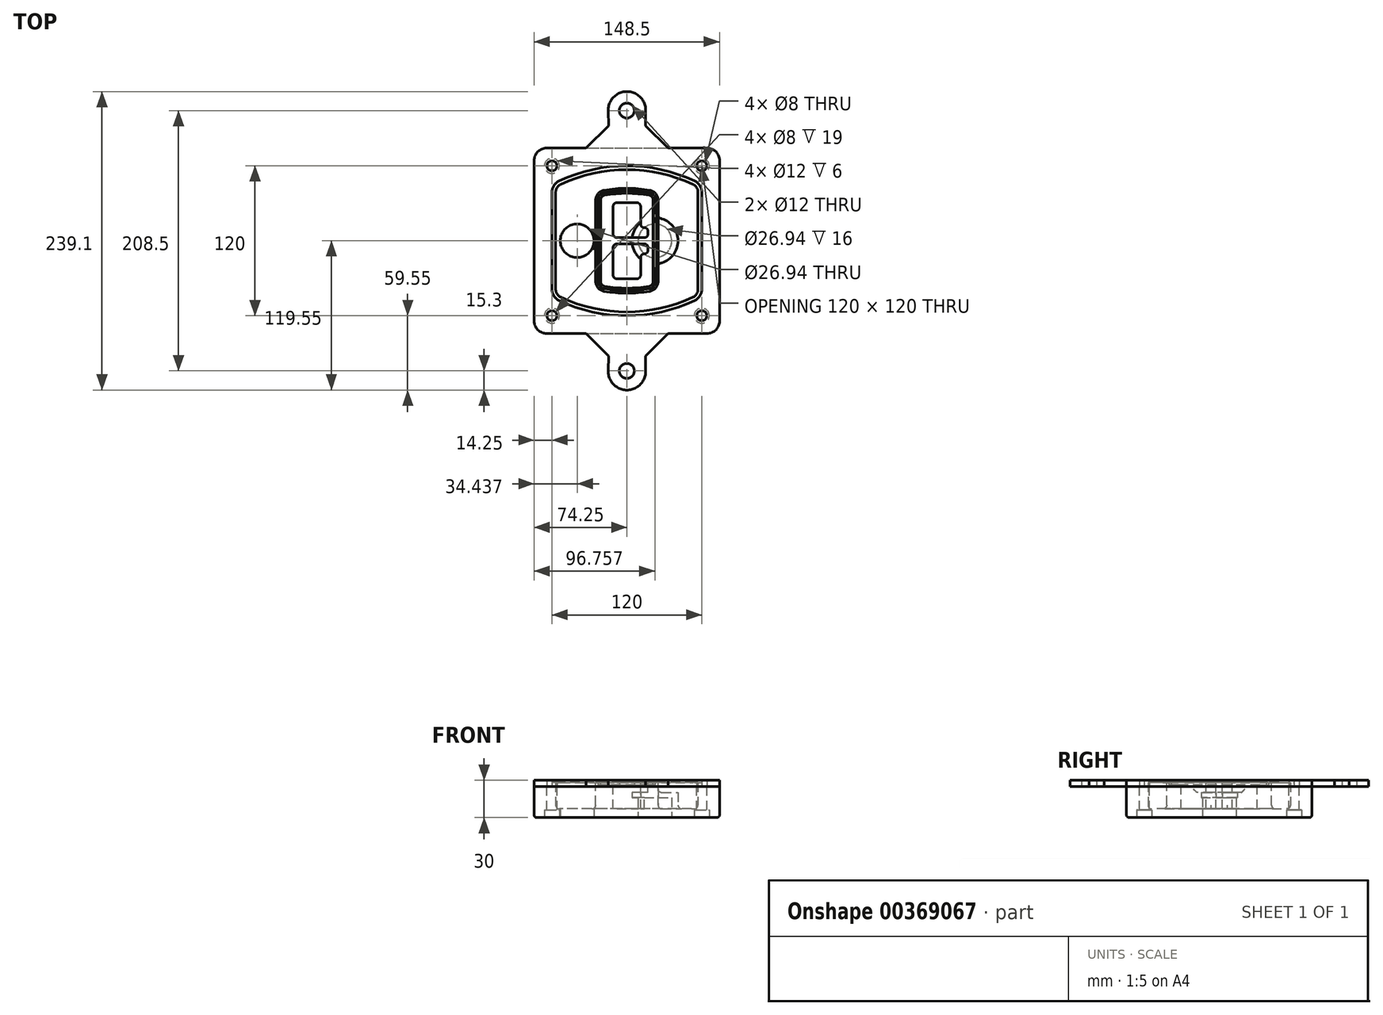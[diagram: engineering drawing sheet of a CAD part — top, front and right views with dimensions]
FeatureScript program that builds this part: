
annotation { "Feature Type Name" : "Feature", "Feature Type Description" : "" }
export const myFeature = defineFeature(function(context is Context, id is Id, definition is map)
    precondition{}
    {
        {
            var Q0;
            Q0=qCreatedBy(makeId("Top.planeOp"),FACE);
            var sketch = newSketch(context, id + "F0", { "sketchPlane" : qUnion([Q0])});
            skPoint(sketch, "E0.rect.middle", {"position": v(0, 0) * mm});
            skLineSegment(sketch, "E1.bottom", {"start": v(-64.25, -74.25) * mm, "end": v(64.25, -74.25) * mm});
            skLineSegment(sketch, "E1.top", {"start": v(-64.25, 74.25) * mm, "end": v(64.25, 74.25) * mm});
            skLineSegment(sketch, "E1.left", {"start": v(-74.25, -64.25) * mm, "end": v(-74.25, 64.25) * mm});
            skLineSegment(sketch, "E1.right", {"start": v(74.25, -64.25) * mm, "end": v(74.25, 64.25) * mm});
            skLineSegment(sketch, "E2", {"start": v(-74.25, 74.25) * mm, "end": v(74.25, -74.25) * mm, "construction": true});
            skLineSegment(sketch, "E3", {"start": v(74.25, 74.25) * mm, "end": v(-74.25, -74.25) * mm, "construction": true});
            skCircle(sketch, "E4", {"center": v(-60, 60) * mm, "radius": 4 * mm});
            skCircle(sketch, "E5", {"center": v(60, 60) * mm, "radius": 4 * mm});
            skCircle(sketch, "E6", {"center": v(60, -60) * mm, "radius": 4 * mm});
            skCircle(sketch, "E7", {"center": v(-60, -60) * mm, "radius": 4 * mm});
            skLineSegment(sketch, "E8", {"start": v(-60, 60) * mm, "end": v(60, 60) * mm, "construction": true});
            skLineSegment(sketch, "E9", {"start": v(60, 60) * mm, "end": v(60, -60) * mm, "construction": true});
            skLineSegment(sketch, "E10", {"start": v(60, -60) * mm, "end": v(-60, -60) * mm, "construction": true});
            skLineSegment(sketch, "E11", {"start": v(-60, -60) * mm, "end": v(-60, 60) * mm, "construction": true});
            skLineSegment(sketch, "E12", {"start": v(-60, 38.83) * mm, "end": v(-60, -38.83) * mm});
            skLineSegment(sketch, "E13", {"start": v(60, 38.83) * mm, "end": v(60, -38.83) * mm});
            skArc(sketch, "E14", {"start": v(54.26, 47.88) * mm, "mid": v(0, 60) * mm, "end": v(-54.26, 47.88) * mm});
            skArc(sketch, "E15", {"start": v(-54.26, -47.88) * mm, "mid": v(0, -60) * mm, "end": v(54.26, -47.88) * mm});
            skLineSegment(sketch, "E16", {"start": v(-60, 0) * mm, "end": v(60, 0) * mm, "construction": true});
            skPoint(sketch, "E17.visualSharp", {"position": v(-60, -45) * mm});
            skArc(sketch, "E17.filletArc", {"start": v(-60, -38.83) * mm, "mid": v(-58.44, -44.2) * mm, "end": v(-54.26, -47.88) * mm});
            skPoint(sketch, "E18.visualSharp", {"position": v(-60, 45) * mm});
            skArc(sketch, "E18.filletArc", {"start": v(-54.26, 47.88) * mm, "mid": v(-58.44, 44.2) * mm, "end": v(-60, 38.83) * mm});
            skPoint(sketch, "E19.visualSharp", {"position": v(60, 45) * mm});
            skArc(sketch, "E19.filletArc", {"start": v(60, 38.83) * mm, "mid": v(58.44, 44.2) * mm, "end": v(54.26, 47.88) * mm});
            skPoint(sketch, "E20.visualSharp", {"position": v(60, -45) * mm});
            skArc(sketch, "E20.filletArc", {"start": v(54.26, -47.88) * mm, "mid": v(58.44, -44.2) * mm, "end": v(60, -38.83) * mm});
            skPoint(sketch, "E21.visualSharp", {"position": v(-74.25, 74.25) * mm});
            skArc(sketch, "E21.filletArc", {"start": v(-64.25, 74.25) * mm, "mid": v(-71.32, 71.32) * mm, "end": v(-74.25, 64.25) * mm});
            skPoint(sketch, "E22.visualSharp", {"position": v(74.25, 74.25) * mm});
            skArc(sketch, "E22.filletArc", {"start": v(74.25, 64.25) * mm, "mid": v(71.32, 71.32) * mm, "end": v(64.25, 74.25) * mm});
            skPoint(sketch, "E23.visualSharp", {"position": v(74.25, -74.25) * mm});
            skArc(sketch, "E23.filletArc", {"start": v(64.25, -74.25) * mm, "mid": v(71.32, -71.32) * mm, "end": v(74.25, -64.25) * mm});
            skPoint(sketch, "E24.visualSharp", {"position": v(-74.25, -74.25) * mm});
            skArc(sketch, "E24.filletArc", {"start": v(-74.25, -64.25) * mm, "mid": v(-71.32, -71.32) * mm, "end": v(-64.25, -74.25) * mm});
            skArc(sketch, "E25.0", {"start": v(57, 38.83) * mm, "mid": v(55.9, 42.58) * mm, "end": v(52.98, 45.17) * mm});
            skLineSegment(sketch, "E25.1", {"start": v(57, 38.83) * mm, "end": v(57, -38.83) * mm});
            skArc(sketch, "E25.2", {"start": v(52.98, -45.17) * mm, "mid": v(55.9, -42.58) * mm, "end": v(57, -38.83) * mm});
            skArc(sketch, "E25.3", {"start": v(-52.98, -45.17) * mm, "mid": v(0, -57) * mm, "end": v(52.98, -45.17) * mm});
            skArc(sketch, "E25.4", {"start": v(-57, -38.83) * mm, "mid": v(-55.9, -42.58) * mm, "end": v(-52.98, -45.17) * mm});
            skArc(sketch, "E25.5", {"start": v(52.98, 45.17) * mm, "mid": v(0, 57) * mm, "end": v(-52.98, 45.17) * mm});
            skLineSegment(sketch, "E25.6", {"start": v(-57, 38.83) * mm, "end": v(-57, -38.83) * mm});
            skArc(sketch, "E25.7", {"start": v(-52.98, 45.17) * mm, "mid": v(-55.9, 42.58) * mm, "end": v(-57, 38.83) * mm});
            skArc(sketch, "E26.0", {"start": v(-55.96, 51.5) * mm, "mid": v(-61.82, 46.33) * mm, "end": v(-64, 38.83) * mm});
            skArc(sketch, "E26.1", {"start": v(55.96, 51.5) * mm, "mid": v(0, 64) * mm, "end": v(-55.96, 51.5) * mm});
            skArc(sketch, "E26.2", {"start": v(64, 38.83) * mm, "mid": v(61.82, 46.33) * mm, "end": v(55.96, 51.5) * mm});
            skLineSegment(sketch, "E26.3", {"start": v(64, 38.83) * mm, "end": v(64, -38.83) * mm});
            skArc(sketch, "E26.4", {"start": v(55.96, -51.5) * mm, "mid": v(61.82, -46.33) * mm, "end": v(64, -38.83) * mm});
            skLineSegment(sketch, "E26.5", {"start": v(-64, 38.83) * mm, "end": v(-64, -38.83) * mm});
            skArc(sketch, "E26.6", {"start": v(-55.96, -51.5) * mm, "mid": v(0, -64) * mm, "end": v(55.96, -51.5) * mm});
            skArc(sketch, "E26.7", {"start": v(-64, -38.83) * mm, "mid": v(-61.82, -46.33) * mm, "end": v(-55.96, -51.5) * mm});
            skSolve(sketch);
        }
        {
            var Q0;
            Q0=makeQuery(id+"F0.imprint","IMPRINT",FACE,{"disambiguationData":[TD([[makeQuery(id+"F0.imprint","IMPRINT",EDGE,{"derivedFrom":sQuery(id+"F0.wireOp",EDGE,"E1.bottom")}),1.0]])]});
            var Q1;
            Q1=makeQuery(id+"F0.imprint","IMPRINT",FACE,{"disambiguationData":[TD([[makeQuery(id+"F0.imprint","IMPRINT",EDGE,{"derivedFrom":sQuery(id+"F0.wireOp",EDGE,"E12")}),1.0]])]});
            var Q2;
            Q2=makeQuery(id+"F0.imprint","IMPRINT",FACE,{"disambiguationData":[TD([[makeQuery(id+"F0.imprint","IMPRINT",EDGE,{"derivedFrom":sQuery(id+"F0.wireOp",EDGE,"E25.0")}),1.0]])]});
            var Q3;
            Q3=makeQuery(id+"F0.imprint","IMPRINT",FACE,{"disambiguationData":[TD([[makeQuery(id+"F0.imprint","IMPRINT",EDGE,{"derivedFrom":sQuery(id+"F0.wireOp",EDGE,"E12")}),-1.0]])]});
            extrude(context, id + "F1", {"entities" : qUnion([Q0, Q1, Q2, Q3]), "oppositeDirection" : true, "depth" : 25 * mm});
        }
        {
            var Q0;
            Q0=makeQuery(id+"F0.imprint","IMPRINT",FACE,{"disambiguationData":[TD([[makeQuery(id+"F0.imprint","IMPRINT",EDGE,{"derivedFrom":sQuery(id+"F0.wireOp",EDGE,"E12")}),1.0]])]});
            extrude(context, id + "F2", {"entities" : qUnion([Q0]), "operationType" : NewBodyOperationType.ADD, "depth" : 3 * mm});
        }
        {
            var Q0;
            Q0=makeQuery(id+"F0.imprint","IMPRINT",FACE,{"disambiguationData":[TD([[makeQuery(id+"F0.imprint","IMPRINT",EDGE,{"derivedFrom":sQuery(id+"F0.wireOp",EDGE,"E25.0")}),1.0]])]});
            extrude(context, id + "F3", {"entities" : qUnion([Q0]), "operationType" : NewBodyOperationType.REMOVE, "oppositeDirection" : true, "depth" : 18 * mm});
        }
        {
            var Q0;
            Q0=makeQuery(id+"F2.opExtrude","CAP_FACE",FACE,{"disambiguationData":[OSD([sQuery(id+"F0.wireOp",EDGE,"E12"),sQuery(id+"F0.wireOp",EDGE,"E13"),sQuery(id+"F0.wireOp",EDGE,"E14"),sQuery(id+"F0.wireOp",EDGE,"E15"),sQuery(id+"F0.wireOp",EDGE,"E17.filletArc"),sQuery(id+"F0.wireOp",EDGE,"E18.filletArc"),sQuery(id+"F0.wireOp",EDGE,"E19.filletArc"),sQuery(id+"F0.wireOp",EDGE,"E20.filletArc"),sQuery(id+"F0.wireOp",EDGE,"E25.0"),sQuery(id+"F0.wireOp",EDGE,"E25.1"),sQuery(id+"F0.wireOp",EDGE,"E25.2"),sQuery(id+"F0.wireOp",EDGE,"E25.3"),sQuery(id+"F0.wireOp",EDGE,"E25.4"),sQuery(id+"F0.wireOp",EDGE,"E25.5"),sQuery(id+"F0.wireOp",EDGE,"E25.6"),sQuery(id+"F0.wireOp",EDGE,"E25.7")])],"isStart":false});
            var sketch = newSketch(context, id + "F4", { "sketchPlane" : qUnion([Q0])});
            skArc(sketch, "E27.0", {"start": v(-18.34, -40.45) * mm, "mid": v(0, -42) * mm, "end": v(18.34, -40.45) * mm});
            skArc(sketch, "E28.0", {"start": v(18.34, 40.45) * mm, "mid": v(0, 42) * mm, "end": v(-18.34, 40.45) * mm});
            skLineSegment(sketch, "E29", {"start": v(-25, 32.57) * mm, "end": v(-25, -32.57) * mm});
            skLineSegment(sketch, "E30", {"start": v(25, 32.57) * mm, "end": v(25, -32.57) * mm});
            skLineSegment(sketch, "E31", {"start": v(-25, 39.1) * mm, "end": v(25, 39.1) * mm, "construction": true});
            skLineSegment(sketch, "E32", {"start": v(-25, -39.1) * mm, "end": v(25, -39.1) * mm, "construction": true});
            skPoint(sketch, "E33.visualSharp", {"position": v(-25, 39.1) * mm});
            skArc(sketch, "E33.filletArc", {"start": v(-18.34, 40.45) * mm, "mid": v(-23.11, 37.73) * mm, "end": v(-25, 32.57) * mm});
            skPoint(sketch, "E34.visualSharp", {"position": v(25, 39.1) * mm});
            skArc(sketch, "E34.filletArc", {"start": v(25, 32.57) * mm, "mid": v(23.11, 37.73) * mm, "end": v(18.34, 40.45) * mm});
            skPoint(sketch, "E35.visualSharp", {"position": v(25, -39.1) * mm});
            skArc(sketch, "E35.filletArc", {"start": v(18.34, -40.45) * mm, "mid": v(23.11, -37.73) * mm, "end": v(25, -32.57) * mm});
            skPoint(sketch, "E36.visualSharp", {"position": v(-25, -39.1) * mm});
            skArc(sketch, "E36.filletArc", {"start": v(-25, -32.57) * mm, "mid": v(-23.11, -37.73) * mm, "end": v(-18.34, -40.45) * mm});
            skArc(sketch, "E37.0", {"start": v(52.98, 45.17) * mm, "mid": v(0, 57) * mm, "end": v(-52.98, 45.17) * mm});
            skArc(sketch, "E37.1", {"start": v(-52.98, 45.17) * mm, "mid": v(-55.9, 42.58) * mm, "end": v(-57, 38.83) * mm});
            skLineSegment(sketch, "E37.2", {"start": v(-57, 38.83) * mm, "end": v(-57, -38.83) * mm});
            skArc(sketch, "E37.3", {"start": v(-57, -38.83) * mm, "mid": v(-55.9, -42.58) * mm, "end": v(-52.98, -45.17) * mm});
            skArc(sketch, "E37.4", {"start": v(-52.98, -45.17) * mm, "mid": v(0, -57) * mm, "end": v(52.98, -45.17) * mm});
            skArc(sketch, "E37.5", {"start": v(52.98, -45.17) * mm, "mid": v(55.9, -42.58) * mm, "end": v(57, -38.83) * mm});
            skLineSegment(sketch, "E37.6", {"start": v(57, 38.83) * mm, "end": v(57, -38.83) * mm});
            skArc(sketch, "E37.7", {"start": v(57, 38.83) * mm, "mid": v(55.9, 42.58) * mm, "end": v(52.98, 45.17) * mm});
            skLineSegment(sketch, "E38.0", {"start": v(23, 32.57) * mm, "end": v(23, -32.57) * mm});
            skArc(sketch, "E38.1", {"start": v(18, -38.48) * mm, "mid": v(21.58, -36.44) * mm, "end": v(23, -32.57) * mm});
            skArc(sketch, "E38.2", {"start": v(-18, -38.48) * mm, "mid": v(0, -40) * mm, "end": v(18, -38.48) * mm});
            skArc(sketch, "E38.3", {"start": v(-23, -32.57) * mm, "mid": v(-21.58, -36.44) * mm, "end": v(-18, -38.48) * mm});
            skLineSegment(sketch, "E38.4", {"start": v(-23, 32.57) * mm, "end": v(-23, -32.57) * mm});
            skArc(sketch, "E38.5", {"start": v(23, 32.57) * mm, "mid": v(21.58, 36.44) * mm, "end": v(18, 38.48) * mm});
            skArc(sketch, "E38.6", {"start": v(-18, 38.48) * mm, "mid": v(-21.58, 36.44) * mm, "end": v(-23, 32.57) * mm});
            skArc(sketch, "E38.7", {"start": v(18, 38.48) * mm, "mid": v(0, 40) * mm, "end": v(-18, 38.48) * mm});
            skArc(sketch, "E39.0", {"start": v(21, 32.57) * mm, "mid": v(20.06, 35.15) * mm, "end": v(17.67, 36.5) * mm});
            skLineSegment(sketch, "E39.1", {"start": v(21, 32.57) * mm, "end": v(21, -32.57) * mm});
            skArc(sketch, "E39.2", {"start": v(17.67, -36.5) * mm, "mid": v(20.06, -35.15) * mm, "end": v(21, -32.57) * mm});
            skArc(sketch, "E39.3", {"start": v(-17.67, -36.5) * mm, "mid": v(0, -38) * mm, "end": v(17.67, -36.5) * mm});
            skArc(sketch, "E39.4", {"start": v(-21, -32.57) * mm, "mid": v(-20.06, -35.15) * mm, "end": v(-17.67, -36.5) * mm});
            skArc(sketch, "E39.5", {"start": v(17.67, 36.5) * mm, "mid": v(0, 38) * mm, "end": v(-17.67, 36.5) * mm});
            skLineSegment(sketch, "E39.6", {"start": v(-21, 32.57) * mm, "end": v(-21, -32.57) * mm});
            skArc(sketch, "E39.7", {"start": v(-17.67, 36.5) * mm, "mid": v(-20.06, 35.15) * mm, "end": v(-21, 32.57) * mm});
            skLineSegment(sketch, "E40", {"start": v(-25, 0) * mm, "end": v(25, 0) * mm, "construction": true});
            skLineSegment(sketch, "E41", {"start": v(-11, 5.5) * mm, "end": v(-11, 27.5) * mm});
            skLineSegment(sketch, "E42", {"start": v(-8, 30.5) * mm, "end": v(8, 30.5) * mm});
            skLineSegment(sketch, "E43", {"start": v(11, 27.5) * mm, "end": v(11, 13.5) * mm});
            skLineSegment(sketch, "E44", {"start": v(14, 10.5) * mm, "end": v(14, 10.5) * mm});
            skLineSegment(sketch, "E45", {"start": v(17, 7.5) * mm, "end": v(17, 5.5) * mm});
            skLineSegment(sketch, "E46", {"start": v(14, 2.5) * mm, "end": v(-8, 2.5) * mm});
            skPoint(sketch, "E47.visualSharp", {"position": v(-11, 30.5) * mm});
            skArc(sketch, "E47.filletArc", {"start": v(-8, 30.5) * mm, "mid": v(-10.12, 29.62) * mm, "end": v(-11, 27.5) * mm});
            skPoint(sketch, "E48.visualSharp", {"position": v(11, 30.5) * mm});
            skArc(sketch, "E48.filletArc", {"start": v(11, 27.5) * mm, "mid": v(10.12, 29.62) * mm, "end": v(8, 30.5) * mm});
            skPoint(sketch, "E49.visualSharp", {"position": v(11, 10.5) * mm});
            skArc(sketch, "E49.filletArc", {"start": v(11, 13.5) * mm, "mid": v(11.88, 11.38) * mm, "end": v(14, 10.5) * mm});
            skPoint(sketch, "E50.visualSharp", {"position": v(17, 10.5) * mm});
            skArc(sketch, "E50.filletArc", {"start": v(17, 7.5) * mm, "mid": v(16.12, 9.62) * mm, "end": v(14, 10.5) * mm});
            skPoint(sketch, "E51.visualSharp", {"position": v(17, 2.5) * mm});
            skArc(sketch, "E51.filletArc", {"start": v(14, 2.5) * mm, "mid": v(16.12, 3.38) * mm, "end": v(17, 5.5) * mm});
            skPoint(sketch, "E52.visualSharp", {"position": v(-11, 2.5) * mm});
            skArc(sketch, "E52.filletArc", {"start": v(-11, 5.5) * mm, "mid": v(-10.12, 3.38) * mm, "end": v(-8, 2.5) * mm});
            skLineSegment(sketch, "E53.0.MirrorCS", {"start": v(14, -2.5) * mm, "end": v(-8, -2.5) * mm});
            skArc(sketch, "E54.0.MirrorCS", {"start": v(-11, -5.5) * mm, "mid": v(-10.12, -3.38) * mm, "end": v(-8, -2.5) * mm});
            skLineSegment(sketch, "E55.0.MirrorCS", {"start": v(-11, -5.5) * mm, "end": v(-11, -27.5) * mm});
            skArc(sketch, "E56.0.MirrorCS", {"start": v(-8, -30.5) * mm, "mid": v(-10.12, -29.62) * mm, "end": v(-11, -27.5) * mm});
            skLineSegment(sketch, "E57.0.MirrorCS", {"start": v(-8, -30.5) * mm, "end": v(8, -30.5) * mm});
            skArc(sketch, "E58.0.MirrorCS", {"start": v(11, -27.5) * mm, "mid": v(10.12, -29.62) * mm, "end": v(8, -30.5) * mm});
            skLineSegment(sketch, "E59.0.MirrorCS", {"start": v(11, -27.5) * mm, "end": v(11, -13.5) * mm});
            skArc(sketch, "E60.0.MirrorCS", {"start": v(11, -13.5) * mm, "mid": v(11.88, -11.38) * mm, "end": v(14, -10.5) * mm});
            skArc(sketch, "E61.0.MirrorCS", {"start": v(17, -7.5) * mm, "mid": v(16.12, -9.62) * mm, "end": v(14, -10.5) * mm});
            skLineSegment(sketch, "E62.0.MirrorCS", {"start": v(17, -7.5) * mm, "end": v(17, -5.5) * mm});
            skArc(sketch, "E63.0.MirrorCS", {"start": v(14, -2.5) * mm, "mid": v(16.12, -3.38) * mm, "end": v(17, -5.5) * mm});
            skSolve(sketch);
        }
        {
            var Q0;
            Q0=makeQuery(id+"F4.imprint","IMPRINT",FACE,{"disambiguationData":[TD([[makeQuery(id+"F4.imprint","IMPRINT",EDGE,{"derivedFrom":sQuery(id+"F4.wireOp",EDGE,"E27.0")}),1.0]])]});
            var Q1;
            Q1=makeQuery(id+"F4.imprint","IMPRINT",FACE,{"disambiguationData":[TD([[makeQuery(id+"F4.imprint","IMPRINT",EDGE,{"derivedFrom":sQuery(id+"F4.wireOp",EDGE,"E38.0")}),-1.0]])]});
            var Q2;
            Q2=makeQuery(id+"F4.imprint","IMPRINT",FACE,{"disambiguationData":[TD([[makeQuery(id+"F4.imprint","IMPRINT",EDGE,{"derivedFrom":sQuery(id+"F4.wireOp",EDGE,"E39.0")}),1.0]])]});
            extrude(context, id + "F5", {"entities" : qUnion([Q0, Q1, Q2]), "operationType" : NewBodyOperationType.ADD, "endBound" : BoundingType.UP_TO_NEXT, "oppositeDirection" : true, "depth" : 25 * mm});
        }
        {
            var Q0;
            Q0=makeQuery(id+"F4.imprint","IMPRINT",FACE,{"disambiguationData":[TD([[makeQuery(id+"F4.imprint","IMPRINT",EDGE,{"derivedFrom":sQuery(id+"F4.wireOp",EDGE,"E38.0")}),-1.0]])]});
            extrude(context, id + "F6", {"entities" : qUnion([Q0]), "operationType" : NewBodyOperationType.REMOVE, "oppositeDirection" : true, "depth" : 2 * mm});
        }
        {
            var Q0;
            Q0=makeQuery(id+"F1.opExtrude","CAP_FACE",FACE,{"disambiguationData":[OSD([sQuery(id+"F0.wireOp",EDGE,"E1.bottom"),sQuery(id+"F0.wireOp",EDGE,"E1.top"),sQuery(id+"F0.wireOp",EDGE,"E1.left"),sQuery(id+"F0.wireOp",EDGE,"E1.right"),sQuery(id+"F0.wireOp",EDGE,"E4"),sQuery(id+"F0.wireOp",EDGE,"E5"),sQuery(id+"F0.wireOp",EDGE,"E6"),sQuery(id+"F0.wireOp",EDGE,"E7"),sQuery(id+"F0.wireOp",EDGE,"E21.filletArc"),sQuery(id+"F0.wireOp",EDGE,"E22.filletArc"),sQuery(id+"F0.wireOp",EDGE,"E23.filletArc"),sQuery(id+"F0.wireOp",EDGE,"E24.filletArc")])],"isStart":false});
            var sketch = newSketch(context, id + "F7", { "sketchPlane" : qUnion([Q0])});
            skCircle(sketch, "E64", {"center": v(22.5, 0) * mm, "radius": 13.47 * mm});
            skCircle(sketch, "E65", {"center": v(-39.81, 0) * mm, "radius": 13.47 * mm});
            skLineSegment(sketch, "E66", {"start": v(74.25, 0) * mm, "end": v(-74.25, 0) * mm});
            skCircle(sketch, "E67", {"center": v(22.5, 0) * mm, "radius": 18.47 * mm});
            skCircle(sketch, "E68", {"center": v(60, -60) * mm, "radius": 6 * mm});
            skCircle(sketch, "E69", {"center": v(-60, -60) * mm, "radius": 6 * mm});
            skCircle(sketch, "E70", {"center": v(-60, 60) * mm, "radius": 6 * mm});
            skCircle(sketch, "E71", {"center": v(60, 60) * mm, "radius": 6 * mm});
            skSolve(sketch);
        }
        {
            var Q0;
            {var subQ1=sQuery(id+"F7.wireOp",EDGE,"E66");var subQ4=sQuery(id+"F7.wireOp",EDGE,"E64");var subQ6=makeQuery(id+"F7.imprint","INTERSECT",VERTEX,{"disambiguationData":[OD(0.0)],"derivedFrom":[subQ4,subQ1]});Q0=makeQuery(id+"F7.imprint","IMPRINT",FACE,{"disambiguationData":[TD([[makeQuery(id+"F7.imprint","IMPRINT",EDGE,{"disambiguationData":[TD([[subQ6,-1.0]])],"derivedFrom":subQ4}),-1.0]])]});}
            var Q1;
            {var subQ0=sQuery(id+"F7.wireOp",EDGE,"E66");var subQ1=sQuery(id+"F7.wireOp",EDGE,"E64");var subQ3=makeQuery(id+"F7.imprint","INTERSECT",VERTEX,{"disambiguationData":[OD(0.0)],"derivedFrom":[subQ1,subQ0]});Q1=makeQuery(id+"F7.imprint","IMPRINT",FACE,{"disambiguationData":[TD([[makeQuery(id+"F7.imprint","IMPRINT",EDGE,{"disambiguationData":[TD([[subQ3,-1.0]])],"derivedFrom":subQ1}),1.0]])]});}
            var Q2;
            {var subQ0=sQuery(id+"F7.wireOp",EDGE,"E66");var subQ1=sQuery(id+"F7.wireOp",EDGE,"E64");var subQ3=makeQuery(id+"F7.imprint","INTERSECT",VERTEX,{"disambiguationData":[OD(0.0)],"derivedFrom":[subQ1,subQ0]});Q2=makeQuery(id+"F7.imprint","IMPRINT",FACE,{"disambiguationData":[TD([[makeQuery(id+"F7.imprint","IMPRINT",EDGE,{"disambiguationData":[TD([[subQ3,1.0]])],"derivedFrom":subQ1}),1.0]])]});}
            var Q3;
            {var subQ1=sQuery(id+"F7.wireOp",EDGE,"E66");var subQ4=sQuery(id+"F7.wireOp",EDGE,"E64");var subQ6=makeQuery(id+"F7.imprint","INTERSECT",VERTEX,{"disambiguationData":[OD(0.0)],"derivedFrom":[subQ4,subQ1]});Q3=makeQuery(id+"F7.imprint","IMPRINT",FACE,{"disambiguationData":[TD([[makeQuery(id+"F7.imprint","IMPRINT",EDGE,{"disambiguationData":[TD([[subQ6,1.0]])],"derivedFrom":subQ4}),-1.0]])]});}
            extrude(context, id + "F8", {"entities" : qUnion([Q0, Q1, Q2, Q3]), "operationType" : NewBodyOperationType.ADD, "oppositeDirection" : true, "depth" : 20 * mm});
        }
        {
            var Q0;
            {var subQ0=sQuery(id+"F7.wireOp",EDGE,"E66");var subQ1=sQuery(id+"F7.wireOp",EDGE,"E64");var subQ3=makeQuery(id+"F7.imprint","INTERSECT",VERTEX,{"disambiguationData":[OD(0.0)],"derivedFrom":[subQ1,subQ0]});Q0=makeQuery(id+"F7.imprint","IMPRINT",FACE,{"disambiguationData":[TD([[makeQuery(id+"F7.imprint","IMPRINT",EDGE,{"disambiguationData":[TD([[subQ3,-1.0]])],"derivedFrom":subQ1}),1.0]])]});}
            var Q1;
            {var subQ0=sQuery(id+"F7.wireOp",EDGE,"E66");var subQ1=sQuery(id+"F7.wireOp",EDGE,"E64");var subQ3=makeQuery(id+"F7.imprint","INTERSECT",VERTEX,{"disambiguationData":[OD(0.0)],"derivedFrom":[subQ1,subQ0]});Q1=makeQuery(id+"F7.imprint","IMPRINT",FACE,{"disambiguationData":[TD([[makeQuery(id+"F7.imprint","IMPRINT",EDGE,{"disambiguationData":[TD([[subQ3,1.0]])],"derivedFrom":subQ1}),1.0]])]});}
            extrude(context, id + "F9", {"entities" : qUnion([Q0, Q1]), "operationType" : NewBodyOperationType.REMOVE, "oppositeDirection" : true, "depth" : 16 * mm});
        }
        {
            var Q0;
            {var subQ0=sQuery(id+"F7.wireOp",EDGE,"E66");var subQ1=sQuery(id+"F7.wireOp",EDGE,"E65");var subQ3=makeQuery(id+"F7.imprint","INTERSECT",VERTEX,{"disambiguationData":[OD(0.0)],"derivedFrom":[subQ1,subQ0]});Q0=makeQuery(id+"F7.imprint","IMPRINT",FACE,{"disambiguationData":[TD([[makeQuery(id+"F7.imprint","IMPRINT",EDGE,{"disambiguationData":[TD([[subQ3,-1.0]])],"derivedFrom":subQ1}),1.0]])]});}
            var Q1;
            {var subQ0=sQuery(id+"F7.wireOp",EDGE,"E66");var subQ1=sQuery(id+"F7.wireOp",EDGE,"E65");var subQ3=makeQuery(id+"F7.imprint","INTERSECT",VERTEX,{"disambiguationData":[OD(0.0)],"derivedFrom":[subQ1,subQ0]});Q1=makeQuery(id+"F7.imprint","IMPRINT",FACE,{"disambiguationData":[TD([[makeQuery(id+"F7.imprint","IMPRINT",EDGE,{"disambiguationData":[TD([[subQ3,1.0]])],"derivedFrom":subQ1}),1.0]])]});}
            extrude(context, id + "F10", {"entities" : qUnion([Q0, Q1]), "operationType" : NewBodyOperationType.REMOVE, "oppositeDirection" : true, "depth" : 25 * mm});
        }
        {
            var Q0;
            Q0=makeQuery(id+"F7.imprint","IMPRINT",FACE,{"disambiguationData":[TD([[makeQuery(id+"F7.imprint","IMPRINT",EDGE,{"derivedFrom":sQuery(id+"F7.wireOp",EDGE,"E68")}),1.0]])]});
            var Q1;
            Q1=makeQuery(id+"F7.imprint","IMPRINT",FACE,{"disambiguationData":[TD([[makeQuery(id+"F7.imprint","IMPRINT",EDGE,{"derivedFrom":makeQuery(id+"F1.opExtrude","CAP_EDGE",EDGE,{"disambiguationData":[OSD([sQuery(id+"F0.wireOp",EDGE,"E5")])],"isStart":false})}),-1.0]])]});
            var Q2;
            Q2=makeQuery(id+"F7.imprint","IMPRINT",FACE,{"disambiguationData":[TD([[makeQuery(id+"F7.imprint","IMPRINT",EDGE,{"derivedFrom":sQuery(id+"F7.wireOp",EDGE,"E69")}),1.0]])]});
            var Q3;
            Q3=makeQuery(id+"F7.imprint","IMPRINT",FACE,{"disambiguationData":[TD([[makeQuery(id+"F7.imprint","IMPRINT",EDGE,{"derivedFrom":makeQuery(id+"F1.opExtrude","CAP_EDGE",EDGE,{"disambiguationData":[OSD([sQuery(id+"F0.wireOp",EDGE,"E4")])],"isStart":false})}),-1.0]])]});
            var Q4;
            Q4=makeQuery(id+"F7.imprint","IMPRINT",FACE,{"disambiguationData":[TD([[makeQuery(id+"F7.imprint","IMPRINT",EDGE,{"derivedFrom":sQuery(id+"F7.wireOp",EDGE,"E70")}),1.0]])]});
            var Q5;
            Q5=makeQuery(id+"F7.imprint","IMPRINT",FACE,{"disambiguationData":[TD([[makeQuery(id+"F7.imprint","IMPRINT",EDGE,{"derivedFrom":makeQuery(id+"F1.opExtrude","CAP_EDGE",EDGE,{"disambiguationData":[OSD([sQuery(id+"F0.wireOp",EDGE,"E7")])],"isStart":false})}),-1.0]])]});
            var Q6;
            Q6=makeQuery(id+"F7.imprint","IMPRINT",FACE,{"disambiguationData":[TD([[makeQuery(id+"F7.imprint","IMPRINT",EDGE,{"derivedFrom":sQuery(id+"F7.wireOp",EDGE,"E71")}),1.0]])]});
            var Q7;
            Q7=makeQuery(id+"F7.imprint","IMPRINT",FACE,{"disambiguationData":[TD([[makeQuery(id+"F7.imprint","IMPRINT",EDGE,{"derivedFrom":makeQuery(id+"F1.opExtrude","CAP_EDGE",EDGE,{"disambiguationData":[OSD([sQuery(id+"F0.wireOp",EDGE,"E6")])],"isStart":false})}),-1.0]])]});
            extrude(context, id + "F11", {"entities" : qUnion([Q0, Q1, Q2, Q3, Q4, Q5, Q6, Q7]), "operationType" : NewBodyOperationType.REMOVE, "oppositeDirection" : true, "depth" : 6 * mm});
        }
        {
            var Q0;
            Q0=makeQuery(id+"F9.boolean.opBoolean","COPY",FACE,{"derivedFrom":makeQuery(id+"F9.opExtrude","CAP_FACE",FACE,{"disambiguationData":[OSD([sQuery(id+"F7.wireOp",EDGE,"E64")])],"isStart":false})});
            var sketch = newSketch(context, id + "F12", { "sketchPlane" : qUnion([Q0])});
            skArc(sketch, "E72.0", {"start": v(11, 14.45) * mm, "mid": v(6.45, 9.13) * mm, "end": v(4.2, 2.5) * mm});
            skArc(sketch, "E72.1", {"start": v(4.2, -2.5) * mm, "mid": v(6.45, -9.13) * mm, "end": v(11, -14.45) * mm});
            skLineSegment(sketch, "E73", {"start": v(4.2, -2.5) * mm, "end": v(14, -2.5) * mm});
            skLineSegment(sketch, "E74.0", {"start": v(14, 2.5) * mm, "end": v(4.2, 2.5) * mm});
            skArc(sketch, "E74.1", {"start": v(14, 2.5) * mm, "mid": v(16.12, 3.38) * mm, "end": v(17, 5.5) * mm});
            skLineSegment(sketch, "E74.2", {"start": v(17, 7.5) * mm, "end": v(17, 5.5) * mm});
            skArc(sketch, "E74.3", {"start": v(17, 7.5) * mm, "mid": v(16.12, 9.62) * mm, "end": v(14, 10.5) * mm});
            skArc(sketch, "E74.4", {"start": v(11, 13.5) * mm, "mid": v(11.88, 11.38) * mm, "end": v(14, 10.5) * mm});
            skLineSegment(sketch, "E74.5", {"start": v(11, 14.45) * mm, "end": v(11, 13.5) * mm});
            skLineSegment(sketch, "E74.7", {"start": v(14, -2.5) * mm, "end": v(4.2, -2.5) * mm});
            skArc(sketch, "E74.8", {"start": v(14, -2.5) * mm, "mid": v(16.12, -3.38) * mm, "end": v(17, -5.5) * mm});
            skLineSegment(sketch, "E74.9", {"start": v(17, -7.5) * mm, "end": v(17, -5.5) * mm});
            skArc(sketch, "E74.10", {"start": v(17, -7.5) * mm, "mid": v(16.12, -9.62) * mm, "end": v(14, -10.5) * mm});
            skArc(sketch, "E74.11", {"start": v(11, -13.5) * mm, "mid": v(11.88, -11.38) * mm, "end": v(14, -10.5) * mm});
            skLineSegment(sketch, "E74.12", {"start": v(11, -14.45) * mm, "end": v(11, -13.5) * mm});
            skPoint(sketch, "E75.orphan", {"position": v(11, -27.5) * mm});
            skPoint(sketch, "E76.orphan", {"position": v(-8, -2.5) * mm});
            skPoint(sketch, "E77.orphan", {"position": v(-8, 2.5) * mm});
            skPoint(sketch, "E78.orphan", {"position": v(11, 27.5) * mm});
            skSolve(sketch);
        }
        {
            var Q0;
            {var subQ7=sQuery(id+"F12.wireOp",EDGE,"E72.0");var subQ14=sQuery(id+"F12.wireOp",EDGE,"E72.1");var subQ16=sQuery(id+"F12.wireOp",EDGE,"E74.1");var subQ18=sQuery(id+"F12.wireOp",EDGE,"E74.8");Q0=qUnion([makeQuery(id+"F12.imprint","IMPRINT",FACE,{"disambiguationData":[TD([[makeQuery(id+"F12.imprint","IMPRINT",EDGE,{"derivedFrom":subQ7}),1.0]])]}),makeQuery(id+"F12.imprint","IMPRINT",FACE,{"disambiguationData":[TD([[makeQuery(id+"F12.imprint","IMPRINT",EDGE,{"derivedFrom":subQ14}),1.0]])]}),makeQuery(id+"F12.imprint","IMPRINT",FACE,{"disambiguationData":[TD([[makeQuery(id+"F12.imprint","IMPRINT",EDGE,{"derivedFrom":subQ16}),1.0]])]}),makeQuery(id+"F12.imprint","IMPRINT",FACE,{"disambiguationData":[TD([[makeQuery(id+"F12.imprint","IMPRINT",EDGE,{"derivedFrom":subQ18}),-1.0]])]})]);}
            var Q1;
            Q1=makeQuery(id+"F5.boolean.opBoolean","SPLIT",FACE,{"disambiguationData":[TD([makeQuery(id+"F5.opExtrude","SWEPT_FACE",FACE,{"disambiguationData":[OSD([sQuery(id+"F4.wireOp",EDGE,"E41")])]})])],"derivedFrom":makeQuery(id+"F3.boolean.opBoolean","COPY",FACE,{"derivedFrom":makeQuery(id+"F3.opExtrude","CAP_FACE",FACE,{"disambiguationData":[OSD([sQuery(id+"F0.wireOp",EDGE,"E25.0"),sQuery(id+"F0.wireOp",EDGE,"E25.1"),sQuery(id+"F0.wireOp",EDGE,"E25.2"),sQuery(id+"F0.wireOp",EDGE,"E25.3"),sQuery(id+"F0.wireOp",EDGE,"E25.4"),sQuery(id+"F0.wireOp",EDGE,"E25.5"),sQuery(id+"F0.wireOp",EDGE,"E25.6"),sQuery(id+"F0.wireOp",EDGE,"E25.7")])],"isStart":false})})});
            extrude(context, id + "F13", {"entities" : qUnion([Q0]), "operationType" : NewBodyOperationType.REMOVE, "endBound" : BoundingType.UP_TO_SURFACE, "endBoundEntityFace" : qUnion([Q1]), "depth" : 25 * mm});
        }
        {
            var Q0;
            Q0=makeQuery(id+"F3.boolean.opBoolean","COPY",EDGE,{"derivedFrom":makeQuery(id+"F3.opExtrude","CAP_EDGE",EDGE,{"disambiguationData":[OSD([sQuery(id+"F0.wireOp",EDGE,"E25.6")])],"isStart":false})});
            var Q1;
            Q1=makeQuery(id+"F8.boolean.opBoolean","INTERSECT",EDGE,{"derivedFrom":[makeQuery(id+"F5.opExtrude","SWEPT_FACE",FACE,{"disambiguationData":[OSD([sQuery(id+"F4.wireOp",EDGE,"E30")])]}),makeQuery(id+"F8.opExtrude","CAP_FACE",FACE,{"disambiguationData":[OSD([sQuery(id+"F7.wireOp",EDGE,"E67")])],"isStart":false})]});
            var Q2;
            Q2=makeQuery(id+"F8.boolean.opBoolean","INTERSECT",EDGE,{"disambiguationData":[OD(1.0)],"derivedFrom":[makeQuery(id+"F5.opExtrude","SWEPT_FACE",FACE,{"disambiguationData":[OSD([sQuery(id+"F4.wireOp",EDGE,"E30")])]}),makeQuery(id+"F8.opExtrude","SWEPT_FACE",FACE,{"disambiguationData":[OSD([sQuery(id+"F7.wireOp",EDGE,"E67")])]})]});
            var Q3;
            {var subQ0=sQuery(id+"F4.wireOp",EDGE,"E30");Q3=makeQuery(id+"F8.boolean.opBoolean","SPLIT",EDGE,{"disambiguationData":[TD([makeQuery(id+"F5.opExtrude","SWEPT_FACE",FACE,{"disambiguationData":[OSD([sQuery(id+"F4.wireOp",EDGE,"E35.filletArc")])]})])],"derivedFrom":makeQuery(id+"F5.opExtrude","CAP_EDGE",EDGE,{"disambiguationData":[OSD([subQ0])],"isStart":false})});}
            var Q4;
            {var subQ0=sQuery(id+"F0.wireOp",EDGE,"E25.7");var subQ1=sQuery(id+"F0.wireOp",EDGE,"E25.1");var subQ2=sQuery(id+"F0.wireOp",EDGE,"E25.6");var subQ3=sQuery(id+"F0.wireOp",EDGE,"E25.5");var subQ4=sQuery(id+"F0.wireOp",EDGE,"E25.4");var subQ5=sQuery(id+"F0.wireOp",EDGE,"E25.0");var subQ6=sQuery(id+"F0.wireOp",EDGE,"E25.2");var subQ7=sQuery(id+"F0.wireOp",EDGE,"E25.3");Q4=makeQuery(id+"F8.boolean.opBoolean","INTERSECT",EDGE,{"derivedFrom":[makeQuery(id+"F5.boolean.opBoolean","SPLIT",FACE,{"disambiguationData":[TD([makeQuery(id+"F2.opExtrude","SWEPT_FACE",FACE,{"disambiguationData":[OSD([subQ5])]})])],"derivedFrom":makeQuery(id+"F3.boolean.opBoolean","COPY",FACE,{"derivedFrom":makeQuery(id+"F3.opExtrude","CAP_FACE",FACE,{"disambiguationData":[OSD([subQ5,subQ1,subQ6,subQ7,subQ4,subQ3,subQ2,subQ0])],"isStart":false})})}),makeQuery(id+"F8.opExtrude","SWEPT_FACE",FACE,{"disambiguationData":[OSD([sQuery(id+"F7.wireOp",EDGE,"E67")])]})]});}
            var Q5;
            Q5=makeQuery(id+"F8.boolean.opBoolean","INTERSECT",EDGE,{"disambiguationData":[OD(0.0)],"derivedFrom":[makeQuery(id+"F5.opExtrude","SWEPT_FACE",FACE,{"disambiguationData":[OSD([sQuery(id+"F4.wireOp",EDGE,"E30")])]}),makeQuery(id+"F8.opExtrude","SWEPT_FACE",FACE,{"disambiguationData":[OSD([sQuery(id+"F7.wireOp",EDGE,"E67")])]})]});
            fillet(context, id + "F14", {"entities" : qUnion([Q0, Q1, Q2, Q3, Q4, Q5]), "radius" : 3 * mm, "tangentPropagation" : true, "allowEdgeOverflow" : false});
        }
        {
            var Q0;
            Q0=makeQuery(id+"F1.opExtrude","CAP_EDGE",EDGE,{"disambiguationData":[OSD([sQuery(id+"F0.wireOp",EDGE,"E1.bottom")])],"isStart":false});
            fillet(context, id + "F15", {"entities" : qUnion([Q0]), "radius" : 2 * mm, "tangentPropagation" : true, "allowEdgeOverflow" : false});
        }
        {
            var Q0;
            {var subQ0=sQuery(id+"F0.wireOp",EDGE,"E21.filletArc");var subQ1=sQuery(id+"F0.wireOp",EDGE,"E7");var subQ2=sQuery(id+"F0.wireOp",EDGE,"E6");var subQ3=sQuery(id+"F0.wireOp",EDGE,"E5");var subQ4=sQuery(id+"F0.wireOp",EDGE,"E4");var subQ5=sQuery(id+"F0.wireOp",EDGE,"E22.filletArc");var subQ6=sQuery(id+"F0.wireOp",EDGE,"E1.bottom");var subQ7=sQuery(id+"F0.wireOp",EDGE,"E1.right");var subQ8=sQuery(id+"F0.wireOp",EDGE,"E1.top");var subQ9=sQuery(id+"F0.wireOp",EDGE,"E1.left");var subQ10=sQuery(id+"F0.wireOp",EDGE,"E23.filletArc");var subQ11=sQuery(id+"F0.wireOp",EDGE,"E24.filletArc");Q0=makeQuery(id+"F2.boolean.opBoolean","SPLIT",FACE,{"disambiguationData":[TD([makeQuery(id+"F1.opExtrude","SWEPT_FACE",FACE,{"disambiguationData":[OSD([subQ6])]})])],"derivedFrom":makeQuery(id+"F1.opExtrude","CAP_FACE",FACE,{"disambiguationData":[OSD([subQ6,subQ8,subQ9,subQ7,subQ4,subQ3,subQ2,subQ1,subQ0,subQ5,subQ10,subQ11])],"isStart":true})});}
            var sketch = newSketch(context, id + "F16", { "sketchPlane" : qUnion([Q0])});
            skLineSegment(sketch, "E79", {"start": v(0, 104.25) * mm, "end": v(0, 74.25) * mm, "construction": true});
            skPoint(sketch, "E79.startSnap0", {"position": v(0, 74.25) * mm});
            skCircle(sketch, "E80", {"center": v(0, 104.25) * mm, "radius": 6 * mm});
            skArc(sketch, "E81", {"start": v(15.08, 104.25) * mm, "mid": v(0.09, 119.55) * mm, "end": v(-14.91, 104.25) * mm});
            skLineSegment(sketch, "E82", {"start": v(-14.91, 104.25) * mm, "end": v(-14.67, 92.25) * mm});
            skLineSegment(sketch, "E83", {"start": v(15.08, 104.25) * mm, "end": v(15.08, 92.25) * mm});
            skLineSegment(sketch, "E84", {"start": v(-14.67, 92.25) * mm, "end": v(-32.67, 74.25) * mm});
            skLineSegment(sketch, "E85", {"start": v(15.08, 92.25) * mm, "end": v(33.08, 74.25) * mm});
            skLineSegment(sketch, "E86", {"start": v(-74.25, 0) * mm, "end": v(74.25, 0) * mm, "construction": true});
            skLineSegment(sketch, "E87.MirrorCS", {"start": v(15.08, -104.25) * mm, "end": v(15.08, -92.25) * mm});
            skLineSegment(sketch, "E88.MirrorCS", {"start": v(-14.91, -104.25) * mm, "end": v(-14.67, -92.25) * mm});
            skPoint(sketch, "E89.MirrorP", {"position": v(0, -74.25) * mm});
            skLineSegment(sketch, "E90.MirrorCS", {"start": v(-14.67, -92.25) * mm, "end": v(-32.67, -74.25) * mm});
            skArc(sketch, "E91.MirrorCS", {"start": v(15.08, -104.25) * mm, "mid": v(0.09, -119.55) * mm, "end": v(-14.91, -104.25) * mm});
            skLineSegment(sketch, "E92.MirrorCS", {"start": v(15.08, -92.25) * mm, "end": v(33.08, -74.25) * mm});
            skLineSegment(sketch, "E93.MirrorCS", {"start": v(0, -104.25) * mm, "end": v(0, -74.25) * mm, "construction": true});
            skCircle(sketch, "E94.MirrorC", {"center": v(0, -104.25) * mm, "radius": 6 * mm});
            skSolve(sketch);
        }
        {
            var Q0;
            Q0=makeQuery(id+"F16.imprint","IMPRINT",FACE,{"disambiguationData":[TD([[makeQuery(id+"F16.imprint","IMPRINT",EDGE,{"derivedFrom":makeQuery(id+"F1.opExtrude","CAP_EDGE",EDGE,{"disambiguationData":[OSD([sQuery(id+"F0.wireOp",EDGE,"E1.left")])],"isStart":true})}),-1.0]])]});
            var Q1;
            Q1=makeQuery(id+"F16.imprint","IMPRINT",FACE,{"disambiguationData":[TD([[makeQuery(id+"F16.imprint","IMPRINT",EDGE,{"derivedFrom":sQuery(id+"F16.wireOp",EDGE,"E87.MirrorCS")}),1.0]])]});
            var Q2;
            Q2=makeQuery(id+"F16.imprint","IMPRINT",FACE,{"disambiguationData":[TD([[makeQuery(id+"F16.imprint","IMPRINT",EDGE,{"derivedFrom":sQuery(id+"F16.wireOp",EDGE,"E80")}),-1.0]])]});
            extrude(context, id + "F17", {"entities" : qUnion([Q0, Q1, Q2]), "depth" : 5 * mm});
        }
    });
